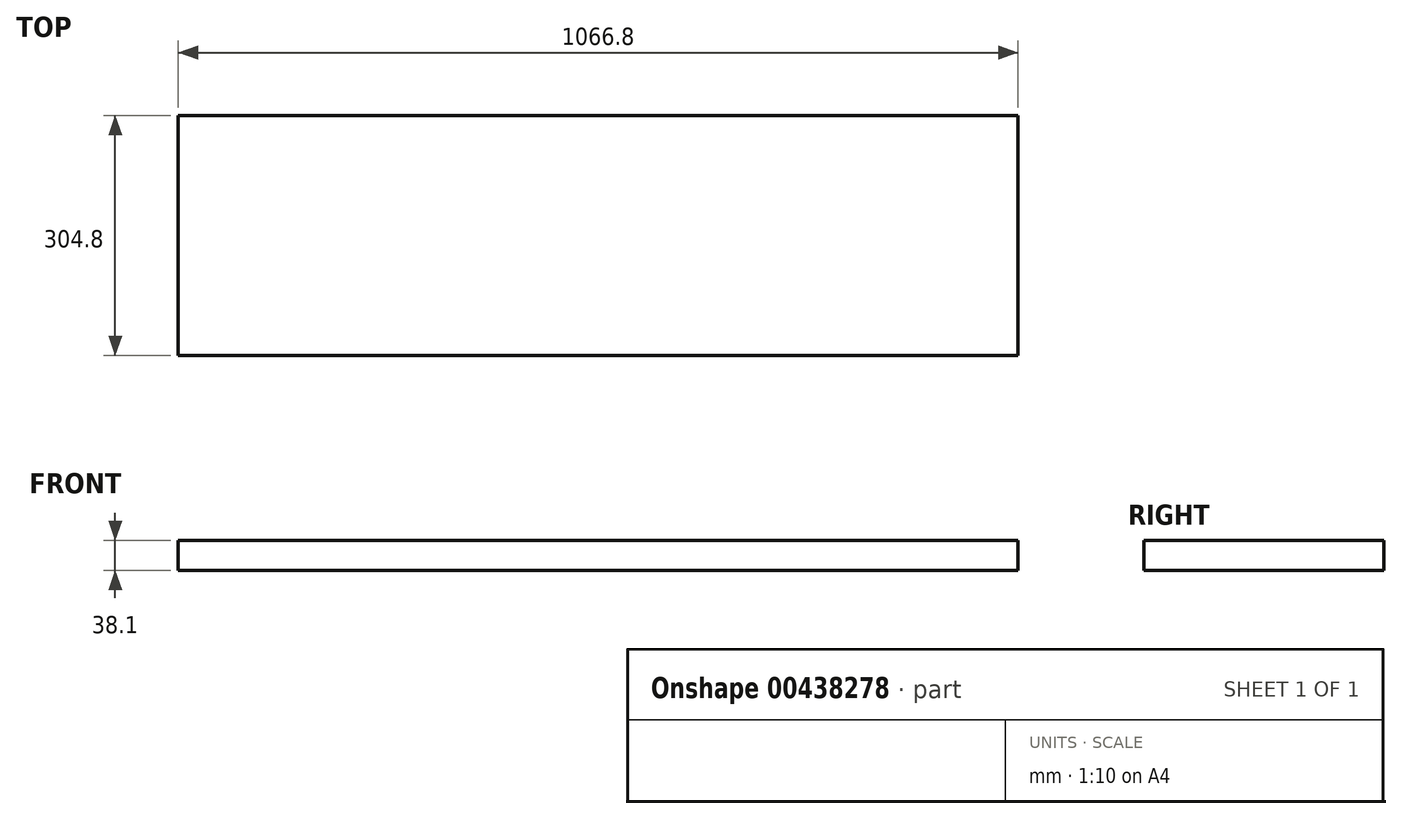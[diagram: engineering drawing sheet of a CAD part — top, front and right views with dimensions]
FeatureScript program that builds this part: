
annotation { "Feature Type Name" : "Feature", "Feature Type Description" : "" }
export const myFeature = defineFeature(function(context is Context, id is Id, definition is map)
    precondition{}
    {
        {
            var Q0;
            Q0=qCreatedBy(makeId("Front.planeOp"),FACE);
            var sketch = newSketch(context, id + "F0", { "sketchPlane" : qUnion([Q0])});
            skLineSegment(sketch, "E0.bottom", {"start": v(-533.4, 19.05) * mm, "end": v(533.4, 19.05) * mm});
            skLineSegment(sketch, "E0.top", {"start": v(-533.4, -19.05) * mm, "end": v(533.4, -19.05) * mm});
            skLineSegment(sketch, "E0.left", {"start": v(-533.4, 19.05) * mm, "end": v(-533.4, -19.05) * mm});
            skLineSegment(sketch, "E0.right", {"start": v(533.4, 19.05) * mm, "end": v(533.4, -19.05) * mm});
            skPoint(sketch, "E0.middle", {"position": v(0, 0) * mm});
            skSolve(sketch);
        }
        {
            var Q0;
            Q0 = qSketchRegion(id + "F0", true);
            extrude(context, id + "F1", {"entities" : qUnion([Q0]), "endBound" : BoundingType.SYMMETRIC, "depth" : 304.8 * mm});
        }
    });
